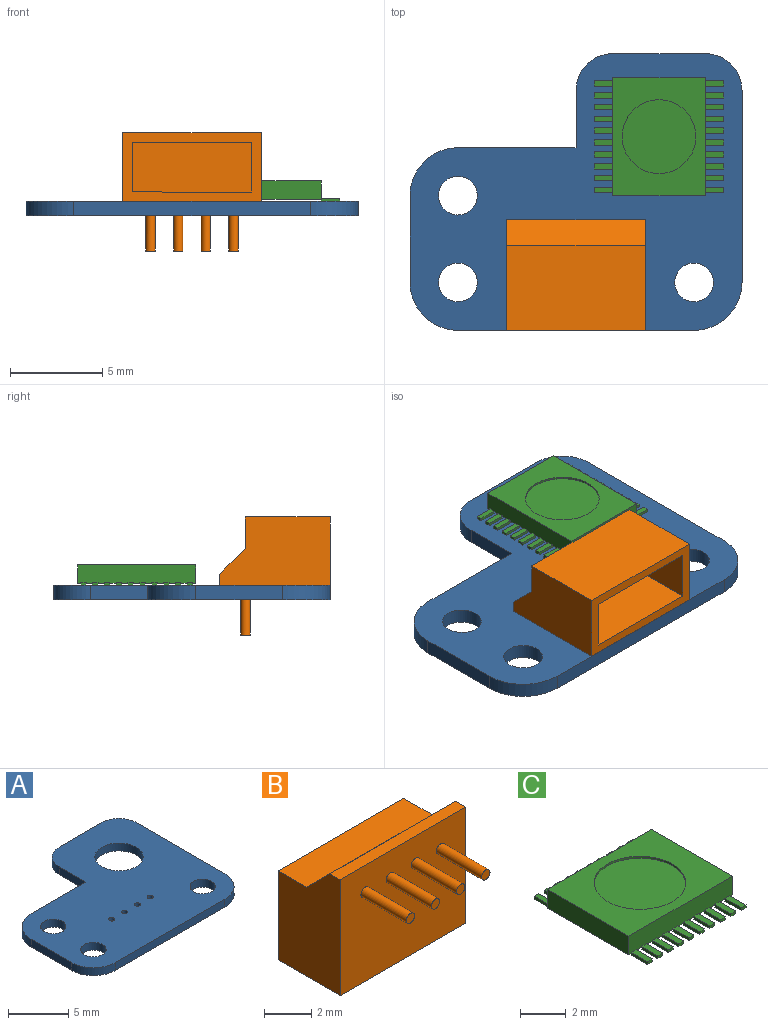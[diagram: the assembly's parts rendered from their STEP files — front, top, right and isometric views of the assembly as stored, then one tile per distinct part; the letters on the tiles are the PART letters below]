
ASSEMBLY  parts=3 mates=2
PART A: 21 faces, bbox 18x15x0.8 mm
  f0: plane 5x0.8mm, normal (0,1,0), area 4mm2, adj f4,f5,f19,f20
  f1: plane 4.7x0.8mm, normal (-1,0,0), area 3.8mm2, adj f4,f5,f16,f17
  f2: plane 12.8x0.8mm, normal (0,-1,0), area 10.2mm2, adj f4,f5,f17,f18
  f3: plane 10.4x0.8mm, normal (1,0,0), area 8.3mm2, adj f4,f5,f18,f20
  f4: plane 18x15mm, normal (0,0,1), area 194.3mm2, adj f0,f1,f2,f3,f6,f7,f8,f9
  f5: plane 18x15mm, normal (0,0,-1), area 194.3mm2, adj f0,f1,f2,f3,f6,f7,f8,f9
  f6: cylinder r=0.25mm len=0.8mm, axis (0,0,-1), area 1.3mm2, adj f4,f5
  f7: cylinder r=0.25mm len=0.8mm, axis (0,0,-1), area 1.3mm2, adj f4,f5
  f8: cylinder r=0.25mm len=0.8mm, axis (0,0,-1), area 1.3mm2, adj f4,f5
  f9: cylinder r=0.25mm len=0.8mm, axis (0,0,-1), area 1.3mm2, adj f4,f5
  f10: cylinder r=1.05mm len=2.1mm, axis (0,0,1), area 5.3mm2, adj f4,f5
  f11: cylinder r=1.05mm len=2.1mm, axis (0,0,1), area 5.3mm2, adj f4,f5
  f12: cylinder r=1.05mm len=2.1mm, axis (0,0,1), area 5.3mm2, adj f4,f5
  f13: plane 6.4x0.8mm, normal (0,1,0), area 5.1mm2, adj f4,f5,f14,f16
  f14: plane 3.1x0.8mm, normal (-1,0,0), area 2.5mm2, adj f4,f5,f13,f19
  f15: cylinder r=2mm len=4mm, axis (0,0,-1), area 10.1mm2, adj f4,f5
  f16: cylinder r=2.6mm len=2.6mm, axis (0,0,-1), area 3.3mm2, adj f1,f4,f5,f13
  f17: cylinder r=2.6mm len=2.6mm, axis (0,0,1), area 3.3mm2, adj f1,f2,f4,f5
  f18: cylinder r=2.6mm len=2.6mm, axis (0,0,-1), area 3.3mm2, adj f2,f3,f4,f5
  f19: cylinder r=2mm len=2mm, axis (0,0,1), area 2.5mm2, adj f0,f4,f5,f14
  f20: cylinder r=2mm len=2mm, axis (0,0,1), area 2.5mm2, adj f0,f3,f4,f5
PART B: 21 faces, bbox 7.5x6.4x6 mm
  f0: plane 7.5x3.7mm, normal (0,0,-1), area 10.2mm2, adj f2,f3,f4,f5,f8,f9,f10,f11
  f1: plane 7.5x1.7mm, normal (0,0,1), area 12.7mm2, adj f2,f4,f5,f7
  f2: plane 6x3.7mm, normal (-1,0,0), area 18.8mm2, adj f0,f1,f3,f5,f6,f7
  f3: plane 7.5x6mm, normal (0,-1,0), area 44.2mm2, adj f0,f2,f4,f6,f13,f15,f17,f19
  f4: plane 6x3.7mm, normal (1,0,0), area 18.8mm2, adj f0,f1,f3,f5,f6,f7
  f5: plane 7.5x4.6mm, normal (0,1,0), area 34.5mm2, adj f0,f1,f2,f4
  f6: plane 7.5x0.6mm, normal (0,0,1), area 4.5mm2, adj f2,f3,f4,f7
  f7: plane 7.5x1.4mm, normal (0,0.71,0.71), area 14.8mm2, adj f1,f2,f4,f6
  f8: plane 4.1x2.7mm, normal (-1,0,0), area 11.1mm2, adj f0,f9,f11,f12
  f9: plane 6.5x4.1mm, normal (0,1,0), area 26.7mm2, adj f0,f8,f10,f12
  f10: plane 4.1x2.7mm, normal (1,0,0), area 11.1mm2, adj f0,f9,f11,f12
  f11: plane 6.5x4.1mm, normal (0,-1,0), area 26.7mm2, adj f0,f8,f10,f12
  f12: plane 6.5x2.7mm, normal (0,0,-1), area 17.6mm2, adj f8,f9,f10,f11
  f13: cylinder r=0.25mm len=2.7mm, axis (0,1,0), area 4.2mm2, adj f3,f14
  f14: plane 0.5x0.5mm, normal (0,-1,0), area 0.2mm2, adj f13
  f15: cylinder r=0.25mm len=2.7mm, axis (0,1,0), area 4.2mm2, adj f3,f16
  f16: plane 0.5x0.5mm, normal (0,-1,0), area 0.2mm2, adj f15
  f17: cylinder r=0.25mm len=2.7mm, axis (0,1,0), area 4.2mm2, adj f3,f18
  f18: plane 0.5x0.5mm, normal (0,-1,0), area 0.2mm2, adj f17
  f19: cylinder r=0.25mm len=2.7mm, axis (0,1,0), area 4.2mm2, adj f3,f20
  f20: plane 0.5x0.5mm, normal (0,-1,0), area 0.2mm2, adj f19
PART C: 128 faces, bbox 6.4x7x1.1 mm
  f0: plane 1x0.3mm, normal (0,0,-1), area 0.3mm2, adj f41,f42,f44,f116
  f1: plane 1x0.3mm, normal (0,0,-1), area 0.3mm2, adj f37,f38,f40,f117
  f2: plane 1x0.3mm, normal (0,0,-1), area 0.3mm2, adj f33,f34,f36,f118
  f3: plane 1x0.3mm, normal (0,0,-1), area 0.3mm2, adj f29,f30,f32,f119
  f4: plane 1x0.3mm, normal (0,0,-1), area 0.3mm2, adj f25,f26,f28,f120
  f5: plane 1x0.3mm, normal (0,0,-1), area 0.3mm2, adj f45,f46,f48,f121
  f6: plane 1x0.3mm, normal (0,0,-1), area 0.3mm2, adj f49,f50,f52,f122
  f7: plane 1x0.3mm, normal (0,0,-1), area 0.3mm2, adj f53,f54,f56,f123
  f8: plane 1x0.3mm, normal (0,0,-1), area 0.3mm2, adj f57,f58,f60,f124
  f9: plane 1x0.3mm, normal (0,0,-1), area 0.3mm2, adj f101,f102,f104,f105
  f10: plane 1x0.3mm, normal (0,0,-1), area 0.3mm2, adj f97,f98,f100,f114
  f11: plane 1x0.3mm, normal (0,0,-1), area 0.3mm2, adj f93,f94,f96,f113
  f12: plane 1x0.3mm, normal (0,0,-1), area 0.3mm2, adj f89,f90,f92,f112
  f13: plane 1x0.3mm, normal (0,0,-1), area 0.3mm2, adj f85,f86,f88,f111
  f14: plane 1x0.3mm, normal (0,0,-1), area 0.3mm2, adj f65,f66,f68,f110
  f15: plane 1x0.3mm, normal (0,0,-1), area 0.3mm2, adj f69,f70,f72,f109
  f16: plane 1x0.3mm, normal (0,0,-1), area 0.3mm2, adj f73,f74,f76,f108
  f17: plane 1x0.3mm, normal (0,0,-1), area 0.3mm2, adj f77,f78,f80,f107
  f18: plane 1x0.3mm, normal (0,0,-1), area 0.3mm2, adj f81,f82,f84,f106
  f19: plane 6.4x1mm, normal (0,1,0), area 6.3mm2, adj f20,f22,f23,f65,f66,f67,f69,f70
  f20: plane 5x1mm, normal (-1,0,0), area 5mm2, adj f19,f21,f23,f125
  f21: plane 6.4x1mm, normal (0,-1,0), area 6.3mm2, adj f20,f22,f23,f25,f26,f27,f29,f30
  f22: plane 5x1mm, normal (1,0,0), area 5mm2, adj f19,f21,f23,f125
  f23: plane 6.4x5mm, normal (0,0,1), area 19.4mm2, adj f19,f20,f21,f22,f126
  f24: plane 1x0.3mm, normal (0,0,-1), area 0.3mm2, adj f61,f62,f64,f115
  f25: plane 1x0.15mm, normal (-1,0,0), area 0.1mm2, adj f4,f21,f27,f28,f120
  f26: plane 1x0.15mm, normal (1,0,0), area 0.1mm2, adj f4,f21,f27,f28,f120
  f27: plane 1x0.3mm, normal (0,0,1), area 0.3mm2, adj f21,f25,f26,f28
  f28: plane 0.3x0.15mm, normal (0,-1,0), area 0mm2, adj f4,f25,f26,f27
  f29: plane 1x0.15mm, normal (-1,0,0), area 0.1mm2, adj f3,f21,f31,f32,f119
  f30: plane 1x0.15mm, normal (1,0,0), area 0.1mm2, adj f3,f21,f31,f32,f119
  f31: plane 1x0.3mm, normal (0,0,1), area 0.3mm2, adj f21,f29,f30,f32
  f32: plane 0.3x0.15mm, normal (0,-1,0), area 0mm2, adj f3,f29,f30,f31
  f33: plane 1x0.15mm, normal (-1,0,0), area 0.1mm2, adj f2,f21,f35,f36,f118
  f34: plane 1x0.15mm, normal (1,0,0), area 0.1mm2, adj f2,f21,f35,f36,f118
  f35: plane 1x0.3mm, normal (0,0,1), area 0.3mm2, adj f21,f33,f34,f36
  f36: plane 0.3x0.15mm, normal (0,-1,0), area 0mm2, adj f2,f33,f34,f35
  f37: plane 1x0.15mm, normal (-1,0,0), area 0.1mm2, adj f1,f21,f39,f40,f117
  f38: plane 1x0.15mm, normal (1,0,0), area 0.1mm2, adj f1,f21,f39,f40,f117
  f39: plane 1x0.3mm, normal (0,0,1), area 0.3mm2, adj f21,f37,f38,f40
  f40: plane 0.3x0.15mm, normal (0,-1,0), area 0mm2, adj f1,f37,f38,f39
  f41: plane 1x0.15mm, normal (-1,0,0), area 0.1mm2, adj f0,f21,f43,f44,f116
  f42: plane 1x0.15mm, normal (1,0,0), area 0.1mm2, adj f0,f21,f43,f44,f116
  f43: plane 1x0.3mm, normal (0,0,1), area 0.3mm2, adj f21,f41,f42,f44
  f44: plane 0.3x0.15mm, normal (0,-1,0), area 0mm2, adj f0,f41,f42,f43
  f45: plane 1x0.15mm, normal (-1,0,0), area 0.1mm2, adj f5,f21,f47,f48,f121
  f46: plane 1x0.15mm, normal (1,0,0), area 0.1mm2, adj f5,f21,f47,f48,f121
  f47: plane 1x0.3mm, normal (0,0,1), area 0.3mm2, adj f21,f45,f46,f48
  f48: plane 0.3x0.15mm, normal (0,-1,0), area 0mm2, adj f5,f45,f46,f47
  f49: plane 1x0.15mm, normal (-1,0,0), area 0.1mm2, adj f6,f21,f51,f52,f122
  f50: plane 1x0.15mm, normal (1,0,0), area 0.1mm2, adj f6,f21,f51,f52,f122
  f51: plane 1x0.3mm, normal (0,0,1), area 0.3mm2, adj f21,f49,f50,f52
  f52: plane 0.3x0.15mm, normal (0,-1,0), area 0mm2, adj f6,f49,f50,f51
  f53: plane 1x0.15mm, normal (-1,0,0), area 0.1mm2, adj f7,f21,f55,f56,f123
  f54: plane 1x0.15mm, normal (1,0,0), area 0.1mm2, adj f7,f21,f55,f56,f123
  f55: plane 1x0.3mm, normal (0,0,1), area 0.3mm2, adj f21,f53,f54,f56
  f56: plane 0.3x0.15mm, normal (0,-1,0), area 0mm2, adj f7,f53,f54,f55
  f57: plane 1x0.15mm, normal (-1,0,0), area 0.1mm2, adj f8,f21,f59,f60,f124
  f58: plane 1x0.15mm, normal (1,0,0), area 0.1mm2, adj f8,f21,f59,f60,f124
  f59: plane 1x0.3mm, normal (0,0,1), area 0.3mm2, adj f21,f57,f58,f60
  f60: plane 0.3x0.15mm, normal (0,-1,0), area 0mm2, adj f8,f57,f58,f59
  f61: plane 1x0.15mm, normal (-1,0,0), area 0.1mm2, adj f21,f24,f63,f64,f115
  f62: plane 1x0.15mm, normal (1,0,0), area 0.1mm2, adj f21,f24,f63,f64,f115
  f63: plane 1x0.3mm, normal (0,0,1), area 0.3mm2, adj f21,f61,f62,f64
  f64: plane 0.3x0.15mm, normal (0,-1,0), area 0mm2, adj f24,f61,f62,f63
  f65: plane 1x0.15mm, normal (1,0,0), area 0.1mm2, adj f14,f19,f67,f68,f110
  f66: plane 1x0.15mm, normal (-1,0,0), area 0.1mm2, adj f14,f19,f67,f68,f110
  f67: plane 1x0.3mm, normal (0,0,1), area 0.3mm2, adj f19,f65,f66,f68
  f68: plane 0.3x0.15mm, normal (0,1,0), area 0mm2, adj f14,f65,f66,f67
  f69: plane 1x0.15mm, normal (1,0,0), area 0.1mm2, adj f15,f19,f71,f72,f109
  f70: plane 1x0.15mm, normal (-1,0,0), area 0.1mm2, adj f15,f19,f71,f72,f109
  f71: plane 1x0.3mm, normal (0,0,1), area 0.3mm2, adj f19,f69,f70,f72
  f72: plane 0.3x0.15mm, normal (0,1,0), area 0mm2, adj f15,f69,f70,f71
  f73: plane 1x0.15mm, normal (1,0,0), area 0.1mm2, adj f16,f19,f75,f76,f108
  f74: plane 1x0.15mm, normal (-1,0,0), area 0.1mm2, adj f16,f19,f75,f76,f108
  f75: plane 1x0.3mm, normal (0,0,1), area 0.3mm2, adj f19,f73,f74,f76
  f76: plane 0.3x0.15mm, normal (0,1,0), area 0mm2, adj f16,f73,f74,f75
  f77: plane 1x0.15mm, normal (1,0,0), area 0.1mm2, adj f17,f19,f79,f80,f107
  f78: plane 1x0.15mm, normal (-1,0,0), area 0.1mm2, adj f17,f19,f79,f80,f107
  f79: plane 1x0.3mm, normal (0,0,1), area 0.3mm2, adj f19,f77,f78,f80
  f80: plane 0.3x0.15mm, normal (0,1,0), area 0mm2, adj f17,f77,f78,f79
  f81: plane 1x0.15mm, normal (1,0,0), area 0.1mm2, adj f18,f19,f83,f84,f106
  f82: plane 1x0.15mm, normal (-1,0,0), area 0.1mm2, adj f18,f19,f83,f84,f106
  f83: plane 1x0.3mm, normal (0,0,1), area 0.3mm2, adj f19,f81,f82,f84
  f84: plane 0.3x0.15mm, normal (0,1,0), area 0mm2, adj f18,f81,f82,f83
  f85: plane 1x0.15mm, normal (1,0,0), area 0.1mm2, adj f13,f19,f87,f88,f111
  f86: plane 1x0.15mm, normal (-1,0,0), area 0.1mm2, adj f13,f19,f87,f88,f111
  f87: plane 1x0.3mm, normal (0,0,1), area 0.3mm2, adj f19,f85,f86,f88
  f88: plane 0.3x0.15mm, normal (0,1,0), area 0mm2, adj f13,f85,f86,f87
  f89: plane 1x0.15mm, normal (1,0,0), area 0.1mm2, adj f12,f19,f91,f92,f112
  f90: plane 1x0.15mm, normal (-1,0,0), area 0.1mm2, adj f12,f19,f91,f92,f112
  f91: plane 1x0.3mm, normal (0,0,1), area 0.3mm2, adj f19,f89,f90,f92
  f92: plane 0.3x0.15mm, normal (0,1,0), area 0mm2, adj f12,f89,f90,f91
  f93: plane 1x0.15mm, normal (1,0,0), area 0.1mm2, adj f11,f19,f95,f96,f113
  f94: plane 1x0.15mm, normal (-1,0,0), area 0.1mm2, adj f11,f19,f95,f96,f113
  f95: plane 1x0.3mm, normal (0,0,1), area 0.3mm2, adj f19,f93,f94,f96
  f96: plane 0.3x0.15mm, normal (0,1,0), area 0mm2, adj f11,f93,f94,f95
  f97: plane 1x0.15mm, normal (1,0,0), area 0.1mm2, adj f10,f19,f99,f100,f114
  f98: plane 1x0.15mm, normal (-1,0,0), area 0.1mm2, adj f10,f19,f99,f100,f114
  f99: plane 1x0.3mm, normal (0,0,1), area 0.3mm2, adj f19,f97,f98,f100
  f100: plane 0.3x0.15mm, normal (0,1,0), area 0mm2, adj f10,f97,f98,f99
  f101: plane 1x0.15mm, normal (1,0,0), area 0.1mm2, adj f9,f19,f103,f104,f105
  f102: plane 1x0.15mm, normal (-1,0,0), area 0.1mm2, adj f9,f19,f103,f104,f105
  f103: plane 1x0.3mm, normal (0,0,1), area 0.3mm2, adj f19,f101,f102,f104
  f104: plane 0.3x0.15mm, normal (0,1,0), area 0mm2, adj f9,f101,f102,f103
  f105: plane 0.3x0.1mm, normal (0,-1,0), area 0mm2, adj f9,f101,f102,f125
  f106: plane 0.3x0.1mm, normal (0,-1,0), area 0mm2, adj f18,f81,f82,f125
  f107: plane 0.3x0.1mm, normal (0,-1,0), area 0mm2, adj f17,f77,f78,f125
  f108: plane 0.3x0.1mm, normal (0,-1,0), area 0mm2, adj f16,f73,f74,f125
  f109: plane 0.3x0.1mm, normal (0,-1,0), area 0mm2, adj f15,f69,f70,f125
  f110: plane 0.3x0.1mm, normal (0,-1,0), area 0mm2, adj f14,f65,f66,f125
  f111: plane 0.3x0.1mm, normal (0,-1,0), area 0mm2, adj f13,f85,f86,f125
  f112: plane 0.3x0.1mm, normal (0,-1,0), area 0mm2, adj f12,f89,f90,f125
  f113: plane 0.3x0.1mm, normal (0,-1,0), area 0mm2, adj f11,f93,f94,f125
  f114: plane 0.3x0.1mm, normal (0,-1,0), area 0mm2, adj f10,f97,f98,f125
  f115: plane 0.3x0.1mm, normal (0,1,0), area 0mm2, adj f24,f61,f62,f125
  f116: plane 0.3x0.1mm, normal (0,1,0), area 0mm2, adj f0,f41,f42,f125
  f117: plane 0.3x0.1mm, normal (0,1,0), area 0mm2, adj f1,f37,f38,f125
  f118: plane 0.3x0.1mm, normal (0,1,0), area 0mm2, adj f2,f33,f34,f125
  f119: plane 0.3x0.1mm, normal (0,1,0), area 0mm2, adj f3,f29,f30,f125
  f120: plane 0.3x0.1mm, normal (0,1,0), area 0mm2, adj f4,f25,f26,f125
  f121: plane 0.3x0.1mm, normal (0,1,0), area 0mm2, adj f5,f45,f46,f125
  f122: plane 0.3x0.1mm, normal (0,1,0), area 0mm2, adj f6,f49,f50,f125
  f123: plane 0.3x0.1mm, normal (0,1,0), area 0mm2, adj f7,f53,f54,f125
  f124: plane 0.3x0.1mm, normal (0,1,0), area 0mm2, adj f8,f57,f58,f125
  f125: plane 6.4x5mm, normal (0,0,-1), area 32mm2, adj f19,f20,f21,f22,f105,f106,f107,f108
  f126: cylinder r=2mm len=4mm, axis (0,0,1), area 1.3mm2, adj f23,f127
  f127: plane 4x4mm, normal (0,0,1), area 12.6mm2, adj f126
PLACE A t=(0,-0.03,0)mm
PLACE B rot(axis=(0,-0.71,-0.71),180deg) t=(12.75,-0.03,0.8)mm
PLACE C rot(axis=(0,0,-1),90deg) t=(11,13.67,0.8)mm
MATE fastened C.f126 <-> A.f15  axis (0,0,1) through (13.5,10.47,1.9)mm
MATE fastened B.f13 <-> A.f6  axis (0,0,1) through (11.25,4.57,0.8)mm
